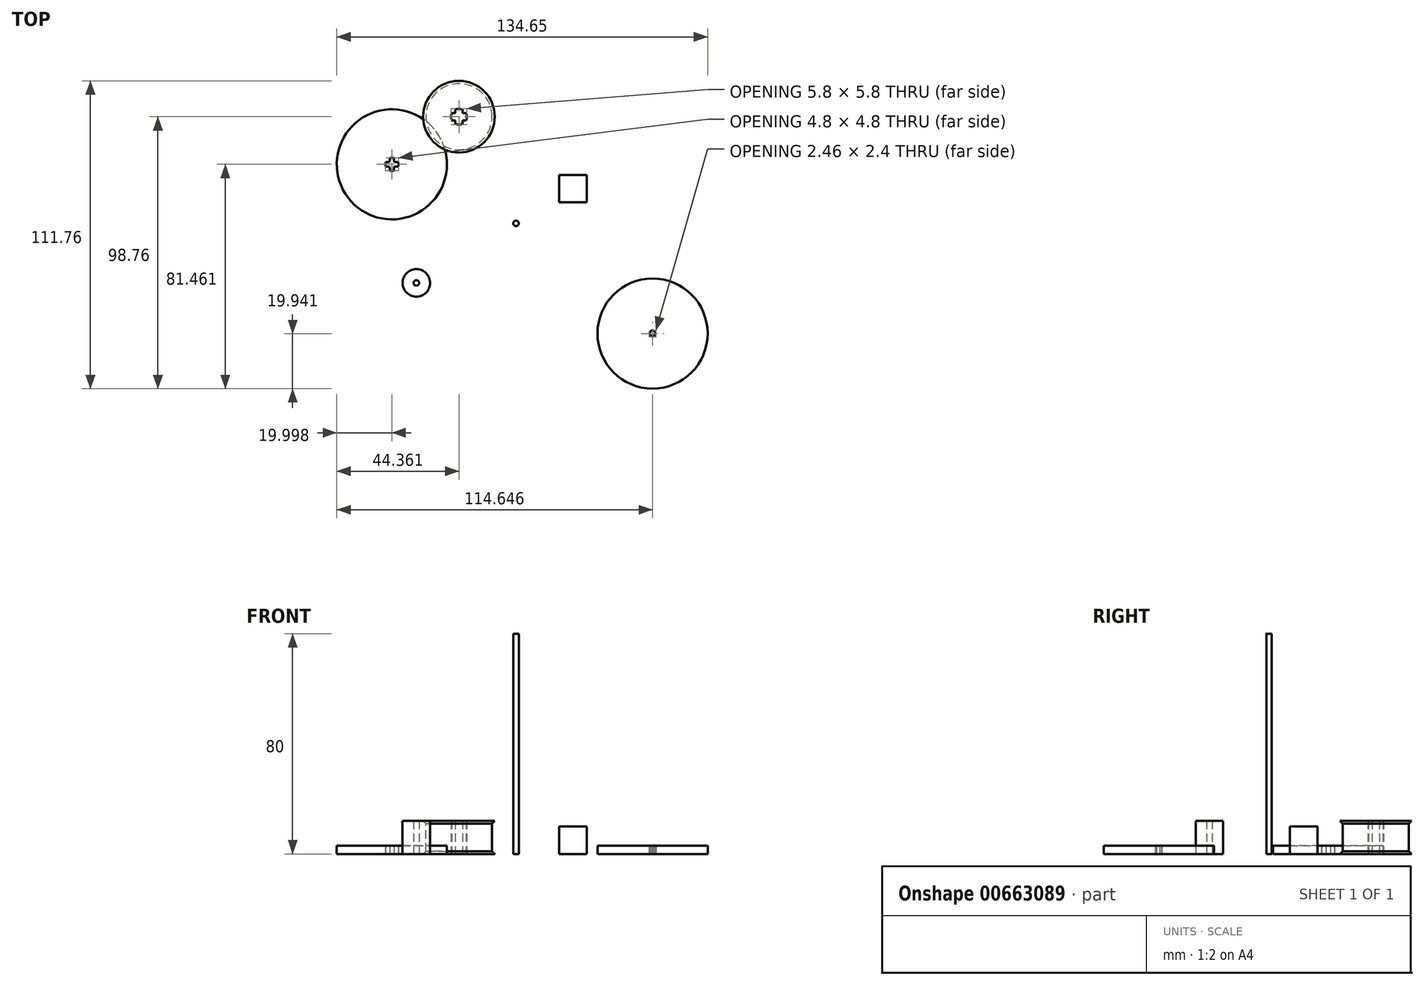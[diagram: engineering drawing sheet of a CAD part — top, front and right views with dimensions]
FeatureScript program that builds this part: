
annotation { "Feature Type Name" : "Feature", "Feature Type Description" : "" }
export const myFeature = defineFeature(function(context is Context, id is Id, definition is map)
    precondition{}
    {
        {
            var Q0;
            Q0=qCreatedBy(makeId("Top.planeOp"),FACE);
            var sketch = newSketch(context, id + "F0", { "sketchPlane" : qUnion([Q0])});
            skCircle(sketch, "E0", {"center": v(18.3, -78.76) * mm, "radius": 20 * mm});
            skCircle(sketch, "E1", {"center": v(18.3, -78.76) * mm, "radius": 0.97 * mm, "construction": true});
            skArc(sketch, "E2", {"start": v(17.76, -77.62) * mm, "mid": v(18.3, -77.78) * mm, "end": v(18.85, -77.62) * mm});
            skArc(sketch, "E3.1.0", {"start": v(17.07, -78.48) * mm, "mid": v(17.54, -78.15) * mm, "end": v(17.76, -77.62) * mm});
            skArc(sketch, "E3.2.0", {"start": v(17.32, -79.54) * mm, "mid": v(17.36, -78.97) * mm, "end": v(17.07, -78.48) * mm});
            skArc(sketch, "E3.3.0", {"start": v(18.3, -80.02) * mm, "mid": v(17.88, -79.64) * mm, "end": v(17.32, -79.54) * mm});
            skArc(sketch, "E3.4.0", {"start": v(19.3, -79.54) * mm, "mid": v(18.73, -79.64) * mm, "end": v(18.3, -80.02) * mm});
            skArc(sketch, "E3.5.0", {"start": v(19.54, -78.48) * mm, "mid": v(19.26, -78.97) * mm, "end": v(19.3, -79.54) * mm});
            skArc(sketch, "E3.6.0", {"start": v(18.85, -77.62) * mm, "mid": v(19.07, -78.15) * mm, "end": v(19.54, -78.48) * mm});
            skSolve(sketch);
        }
        {
            var Q0;
            Q0=makeQuery(id+"F0.imprint","IMPRINT",FACE,{"disambiguationData":[TD([[makeQuery(id+"F0.imprint","IMPRINT",EDGE,{"derivedFrom":sQuery(id+"F0.wireOp",EDGE,"E0")}),1.0]])]});
            extrude(context, id + "F1", {"entities" : qUnion([Q0]), "depth" : 3 * mm, "offsetDistance" : 25 * mm});
        }
        {
            var Q0;
            Q0=qCreatedBy(makeId("Top.planeOp"),FACE);
            var sketch = newSketch(context, id + "F2", { "sketchPlane" : qUnion([Q0])});
            skCircle(sketch, "E4", {"center": v(-31.27, -38.74) * mm, "radius": 1 * mm});
            skSolve(sketch);
        }
        {
            var Q0;
            Q0=makeQuery(id+"F2.imprint","IMPRINT",FACE,{"disambiguationData":[TD([[makeQuery(id+"F2.imprint","IMPRINT",EDGE,{"derivedFrom":sQuery(id+"F2.wireOp",EDGE,"E4")}),1.0]])]});
            extrude(context, id + "F3", {"entities" : qUnion([Q0]), "depth" : 80 * mm, "offsetDistance" : 25 * mm});
        }
        {
            var Q0;
            Q0=qCreatedBy(makeId("Top.planeOp"),FACE);
            var sketch = newSketch(context, id + "F4", { "sketchPlane" : qUnion([Q0])});
            skLineSegment(sketch, "E5.bottom", {"start": v(114.5, -144.93) * mm, "end": v(301.1, -144.93) * mm});
            skLineSegment(sketch, "E5.top", {"start": v(114.5, 146.95) * mm, "end": v(301.1, 146.95) * mm});
            skLineSegment(sketch, "E5.left", {"start": v(114.5, -144.93) * mm, "end": v(114.5, 146.95) * mm});
            skLineSegment(sketch, "E5.right", {"start": v(301.1, -144.93) * mm, "end": v(301.1, 146.95) * mm});
            skSolve(sketch);
        }
        {
            var Q0;
            Q0=makeQuery(id+"F4.imprint","IMPRINT",FACE,{"disambiguationData":[TD([[makeQuery(id+"F4.imprint","IMPRINT",EDGE,{"derivedFrom":sQuery(id+"F4.wireOp",EDGE,"E5.bottom")}),1.0]])]});
            extrude(context, id + "F5", {"entities" : qUnion([Q0]), "depth" : 308 * mm, "offsetDistance" : 25 * mm});
        }
        {
            var Q0;
            Q0=makeQuery(id+"F5.opExtrude","CAP_FACE",FACE,{"disambiguationData":[OSD([sQuery(id+"F4.wireOp",EDGE,"E5.bottom"),sQuery(id+"F4.wireOp",EDGE,"E5.top"),sQuery(id+"F4.wireOp",EDGE,"E5.left"),sQuery(id+"F4.wireOp",EDGE,"E5.right")])],"isStart":false});
            var Q1;
            Q1=makeQuery(id+"F5.opExtrude","CAP_FACE",FACE,{"disambiguationData":[OSD([sQuery(id+"F4.wireOp",EDGE,"E5.bottom"),sQuery(id+"F4.wireOp",EDGE,"E5.top"),sQuery(id+"F4.wireOp",EDGE,"E5.left"),sQuery(id+"F4.wireOp",EDGE,"E5.right")])],"isStart":true});
            shell(context, id + "F6", {"entities" : qUnion([Q0, Q1]), "thickness" : 2.5 * mm});
        }
        {
            var Q0;
            Q0=qCreatedBy(makeId("Top.planeOp"),FACE);
            var sketch = newSketch(context, id + "F7", { "sketchPlane" : qUnion([Q0])});
            skCircle(sketch, "E6", {"center": v(-67.45, -60.37) * mm, "radius": 5 * mm});
            skCircle(sketch, "E7", {"center": v(-67.45, -60.37) * mm, "radius": 1 * mm});
            skSolve(sketch);
        }
        {
            var Q0;
            Q0=makeQuery(id+"F7.imprint","IMPRINT",FACE,{"disambiguationData":[TD([[makeQuery(id+"F7.imprint","IMPRINT",EDGE,{"derivedFrom":sQuery(id+"F7.wireOp",EDGE,"E6")}),1.0]])]});
            extrude(context, id + "F8", {"entities" : qUnion([Q0]), "depth" : 12 * mm, "offsetDistance" : 25 * mm});
        }
        {
            var Q0;
            Q0=makeQuery(id+"F5.opExtrude","SWEPT_BODY",BODY,{"disambiguationData":[OSD([sQuery(id+"F4.wireOp",EDGE,"E5.bottom"),sQuery(id+"F4.wireOp",EDGE,"E5.top"),sQuery(id+"F4.wireOp",EDGE,"E5.left"),sQuery(id+"F4.wireOp",EDGE,"E5.right")])]});
            deleteBodies(context, id + "F9", {"entities" : qUnion([Q0])});
        }
        {
            var Q0;
            Q0=qCreatedBy(makeId("Front.planeOp"),FACE);
            var sketch = newSketch(context, id + "F10", { "sketchPlane" : qUnion([Q0])});
            skLineSegment(sketch, "E8", {"start": v(-51.98, 12) * mm, "end": v(-51.98, 0) * mm, "construction": true});
            skLineSegment(sketch, "E9", {"start": v(-51.98, 0) * mm, "end": v(-50.98, 0) * mm, "construction": true});
            skLineSegment(sketch, "E10", {"start": v(-39.98, 1) * mm, "end": v(-39.98, 11) * mm});
            skLineSegment(sketch, "E11", {"start": v(-38.98, 12) * mm, "end": v(-50.98, 12) * mm});
            skLineSegment(sketch, "E12", {"start": v(-38.98, 12) * mm, "end": v(-39.98, 11) * mm});
            skLineSegment(sketch, "E13", {"start": v(-39.98, 1) * mm, "end": v(-38.98, 0) * mm});
            skLineSegment(sketch, "E14", {"start": v(-50.98, 12) * mm, "end": v(-50.98, 0) * mm});
            skLineSegment(sketch, "E15", {"start": v(-50.98, 12) * mm, "end": v(-51.98, 12) * mm, "construction": true});
            skLineSegment(sketch, "E16", {"start": v(-50.98, 0) * mm, "end": v(-38.98, 0) * mm});
            skSolve(sketch);
        }
        {
            var Q0;
            Q0=makeQuery(id+"F10.imprint","IMPRINT",FACE,{"disambiguationData":[TD([[makeQuery(id+"F10.imprint","IMPRINT",EDGE,{"derivedFrom":sQuery(id+"F10.wireOp",EDGE,"E10")}),1.0]])]});
            var Q1;
            Q1=sQuery(id+"F10.wireOp",EDGE,"E8");
            revolve(context, id + "F11", {"surfaceOperationType" : NewSurfaceOperationType.NEW, "entities" : qUnion([Q0]), "axis" : qUnion([Q1]), "revolveType" : RevolveType.FULL});
        }
        {
            var Q0;
            Q0=makeQuery(id+"F11.opRevolve","SWEPT_FACE",FACE,{"disambiguationData":[OSD([sQuery(id+"F10.wireOp",EDGE,"E16")])]});
            var sketch = newSketch(context, id + "F12", { "sketchPlane" : qUnion([Q0])});
            skCircle(sketch, "E17.0", {"center": v(-51.98, 0) * mm, "radius": 13 * mm});
            skArc(sketch, "E18", {"start": v(-54.24, 0.8) * mm, "mid": v(-54.34, 0.4) * mm, "end": v(-54.38, 0) * mm, "construction": true});
            skLineSegment(sketch, "E19", {"start": v(-51.98, 2.4) * mm, "end": v(-51.98, -2.4) * mm, "construction": true});
            skLineSegment(sketch, "E20", {"start": v(-49.58, 0) * mm, "end": v(-54.38, 0) * mm, "construction": true});
            skLineSegment(sketch, "E21", {"start": v(-52.78, 2.26) * mm, "end": v(-52.78, 1.2) * mm, "construction": true});
            skLineSegment(sketch, "E22", {"start": v(-53.18, 0.8) * mm, "end": v(-54.24, 0.8) * mm, "construction": true});
            skArc(sketch, "E23.trimOffspring", {"start": v(-51.98, 2.4) * mm, "mid": v(-52.38, 2.37) * mm, "end": v(-52.78, 2.26) * mm, "construction": true});
            skPoint(sketch, "E24.visualSharp", {"position": v(-52.78, 0.8) * mm});
            skArc(sketch, "E24.filletArc", {"start": v(-53.18, 0.8) * mm, "mid": v(-52.9, 0.92) * mm, "end": v(-52.78, 1.2) * mm, "construction": true});
            skArc(sketch, "E25.1.0", {"start": v(-54.38, 0) * mm, "mid": v(-54.34, -0.4) * mm, "end": v(-54.24, -0.8) * mm, "construction": true});
            skLineSegment(sketch, "E25.1.1", {"start": v(-54.24, -0.8) * mm, "end": v(-53.18, -0.8) * mm, "construction": true});
            skArc(sketch, "E25.1.2", {"start": v(-52.78, -1.2) * mm, "mid": v(-52.9, -0.92) * mm, "end": v(-53.18, -0.8) * mm, "construction": true});
            skLineSegment(sketch, "E25.1.3", {"start": v(-52.78, -1.2) * mm, "end": v(-52.78, -2.26) * mm, "construction": true});
            skArc(sketch, "E25.1.4", {"start": v(-52.78, -2.26) * mm, "mid": v(-52.38, -2.37) * mm, "end": v(-51.98, -2.4) * mm, "construction": true});
            skArc(sketch, "E25.2.0", {"start": v(-51.98, -2.4) * mm, "mid": v(-51.57, -2.37) * mm, "end": v(-51.18, -2.26) * mm, "construction": true});
            skLineSegment(sketch, "E25.2.1", {"start": v(-51.18, -2.26) * mm, "end": v(-51.18, -1.2) * mm, "construction": true});
            skArc(sketch, "E25.2.2", {"start": v(-50.78, -0.8) * mm, "mid": v(-51.06, -0.92) * mm, "end": v(-51.18, -1.2) * mm, "construction": true});
            skLineSegment(sketch, "E25.2.3", {"start": v(-50.78, -0.8) * mm, "end": v(-49.72, -0.8) * mm, "construction": true});
            skArc(sketch, "E25.2.4", {"start": v(-49.72, -0.8) * mm, "mid": v(-49.61, -0.4) * mm, "end": v(-49.58, 0) * mm, "construction": true});
            skArc(sketch, "E25.3.0", {"start": v(-49.58, 0) * mm, "mid": v(-49.61, 0.4) * mm, "end": v(-49.72, 0.8) * mm, "construction": true});
            skLineSegment(sketch, "E25.3.1", {"start": v(-49.72, 0.8) * mm, "end": v(-50.78, 0.8) * mm, "construction": true});
            skArc(sketch, "E25.3.2", {"start": v(-51.18, 1.2) * mm, "mid": v(-51.06, 0.92) * mm, "end": v(-50.78, 0.8) * mm, "construction": true});
            skLineSegment(sketch, "E25.3.3", {"start": v(-51.18, 1.2) * mm, "end": v(-51.18, 2.26) * mm, "construction": true});
            skArc(sketch, "E25.3.4", {"start": v(-51.18, 2.26) * mm, "mid": v(-51.57, 2.37) * mm, "end": v(-51.98, 2.4) * mm, "construction": true});
            skArc(sketch, "E26.0", {"start": v(-50.68, 2.6) * mm, "mid": v(-51.31, 2.82) * mm, "end": v(-51.98, 2.9) * mm});
            skLineSegment(sketch, "E26.1", {"start": v(-50.68, 1.3) * mm, "end": v(-50.68, 2.6) * mm});
            skLineSegment(sketch, "E26.2", {"start": v(-49.39, 1.3) * mm, "end": v(-50.68, 1.3) * mm});
            skArc(sketch, "E26.3", {"start": v(-49.08, 0) * mm, "mid": v(-49.16, 0.67) * mm, "end": v(-49.39, 1.3) * mm});
            skArc(sketch, "E26.4", {"start": v(-49.39, -1.3) * mm, "mid": v(-49.16, -0.67) * mm, "end": v(-49.08, 0) * mm});
            skArc(sketch, "E26.5", {"start": v(-54.88, 0) * mm, "mid": v(-54.8, -0.67) * mm, "end": v(-54.57, -1.3) * mm});
            skArc(sketch, "E26.6", {"start": v(-54.57, 1.3) * mm, "mid": v(-54.8, 0.67) * mm, "end": v(-54.88, 0) * mm});
            skLineSegment(sketch, "E26.7", {"start": v(-53.28, 1.3) * mm, "end": v(-54.57, 1.3) * mm});
            skLineSegment(sketch, "E26.8", {"start": v(-53.28, 2.6) * mm, "end": v(-53.28, 1.3) * mm});
            skLineSegment(sketch, "E26.9", {"start": v(-54.57, -1.3) * mm, "end": v(-53.28, -1.3) * mm});
            skLineSegment(sketch, "E26.10", {"start": v(-53.28, -1.3) * mm, "end": v(-53.28, -2.6) * mm});
            skArc(sketch, "E26.11", {"start": v(-53.28, -2.6) * mm, "mid": v(-52.65, -2.82) * mm, "end": v(-51.98, -2.9) * mm});
            skArc(sketch, "E26.12", {"start": v(-51.98, -2.9) * mm, "mid": v(-51.31, -2.82) * mm, "end": v(-50.68, -2.6) * mm});
            skLineSegment(sketch, "E26.13", {"start": v(-50.68, -2.6) * mm, "end": v(-50.68, -1.3) * mm});
            skArc(sketch, "E26.14", {"start": v(-51.98, 2.9) * mm, "mid": v(-52.65, 2.82) * mm, "end": v(-53.28, 2.6) * mm});
            skLineSegment(sketch, "E26.15", {"start": v(-50.68, -1.3) * mm, "end": v(-49.39, -1.3) * mm});
            skSolve(sketch);
        }
        {
            var Q0;
            Q0=makeQuery(id+"F12.imprint","IMPRINT",FACE,{"disambiguationData":[TD([[makeQuery(id+"F12.imprint","IMPRINT",EDGE,{"derivedFrom":sQuery(id+"F12.wireOp",EDGE,"E26.0")}),1.0]])]});
            extrude(context, id + "F13", {"entities" : qUnion([Q0]), "operationType" : NewBodyOperationType.REMOVE, "endBound" : BoundingType.THROUGH_ALL, "oppositeDirection" : true, "depth" : 8 * mm, "offsetDistance" : 25 * mm});
        }
        {
            var Q0;
            Q0=qCreatedBy(makeId("Top.planeOp"),FACE);
            var sketch = newSketch(context, id + "F14", { "sketchPlane" : qUnion([Q0])});
            skArc(sketch, "E27", {"start": v(-78.6, -16.5) * mm, "mid": v(-78.7, -16.9) * mm, "end": v(-78.74, -17.3) * mm});
            skLineSegment(sketch, "E28", {"start": v(-76.34, -14.9) * mm, "end": v(-76.34, -19.7) * mm, "construction": true});
            skLineSegment(sketch, "E29", {"start": v(-73.94, -17.3) * mm, "end": v(-78.74, -17.3) * mm, "construction": true});
            skLineSegment(sketch, "E30", {"start": v(-77.14, -15.04) * mm, "end": v(-77.14, -16.1) * mm});
            skLineSegment(sketch, "E31", {"start": v(-77.54, -16.5) * mm, "end": v(-78.6, -16.5) * mm});
            skArc(sketch, "E32.trimOffspring", {"start": v(-76.34, -14.9) * mm, "mid": v(-76.75, -14.93) * mm, "end": v(-77.14, -15.04) * mm});
            skPoint(sketch, "E33.visualSharp", {"position": v(-77.14, -16.5) * mm});
            skArc(sketch, "E33.filletArc", {"start": v(-77.54, -16.5) * mm, "mid": v(-77.26, -16.38) * mm, "end": v(-77.14, -16.1) * mm});
            skArc(sketch, "E34.1.0", {"start": v(-78.74, -17.3) * mm, "mid": v(-78.7, -17.7) * mm, "end": v(-78.6, -18.1) * mm});
            skLineSegment(sketch, "E34.1.1", {"start": v(-78.6, -18.1) * mm, "end": v(-77.54, -18.1) * mm});
            skArc(sketch, "E34.1.2", {"start": v(-77.14, -18.5) * mm, "mid": v(-77.26, -18.22) * mm, "end": v(-77.54, -18.1) * mm});
            skLineSegment(sketch, "E34.1.3", {"start": v(-77.14, -18.5) * mm, "end": v(-77.14, -19.56) * mm});
            skArc(sketch, "E34.1.4", {"start": v(-77.14, -19.56) * mm, "mid": v(-76.75, -19.66) * mm, "end": v(-76.34, -19.7) * mm});
            skArc(sketch, "E34.2.0", {"start": v(-76.34, -19.7) * mm, "mid": v(-75.94, -19.66) * mm, "end": v(-75.54, -19.56) * mm});
            skLineSegment(sketch, "E34.2.1", {"start": v(-75.54, -19.56) * mm, "end": v(-75.54, -18.5) * mm});
            skArc(sketch, "E34.2.2", {"start": v(-75.14, -18.1) * mm, "mid": v(-75.43, -18.22) * mm, "end": v(-75.54, -18.5) * mm});
            skLineSegment(sketch, "E34.2.3", {"start": v(-75.14, -18.1) * mm, "end": v(-74.08, -18.1) * mm});
            skArc(sketch, "E34.2.4", {"start": v(-74.08, -18.1) * mm, "mid": v(-73.98, -17.7) * mm, "end": v(-73.94, -17.3) * mm});
            skArc(sketch, "E34.3.0", {"start": v(-73.94, -17.3) * mm, "mid": v(-73.98, -16.9) * mm, "end": v(-74.08, -16.5) * mm});
            skLineSegment(sketch, "E34.3.1", {"start": v(-74.08, -16.5) * mm, "end": v(-75.14, -16.5) * mm});
            skArc(sketch, "E34.3.2", {"start": v(-75.54, -16.1) * mm, "mid": v(-75.43, -16.38) * mm, "end": v(-75.14, -16.5) * mm});
            skLineSegment(sketch, "E34.3.3", {"start": v(-75.54, -16.1) * mm, "end": v(-75.54, -15.04) * mm});
            skArc(sketch, "E34.3.4", {"start": v(-75.54, -15.04) * mm, "mid": v(-75.94, -14.93) * mm, "end": v(-76.34, -14.9) * mm});
            skCircle(sketch, "E35", {"center": v(-76.34, -17.3) * mm, "radius": 20 * mm});
            skSolve(sketch);
        }
        {
            var Q0;
            Q0=makeQuery(id+"F14.imprint","IMPRINT",FACE,{"disambiguationData":[TD([[makeQuery(id+"F14.imprint","IMPRINT",EDGE,{"derivedFrom":sQuery(id+"F14.wireOp",EDGE,"E27")}),-1.0]])]});
            extrude(context, id + "F15", {"entities" : qUnion([Q0]), "depth" : 3 * mm, "offsetDistance" : 25 * mm});
        }
        {
            var Q0;
            Q0=qCreatedBy(makeId("Top.planeOp"),FACE);
            var sketch = newSketch(context, id + "F16", { "sketchPlane" : qUnion([Q0])});
            skLineSegment(sketch, "E36.bottom", {"start": v(-15.58, -21.12) * mm, "end": v(-5.58, -21.12) * mm});
            skLineSegment(sketch, "E36.top", {"start": v(-15.58, -31.12) * mm, "end": v(-5.58, -31.12) * mm});
            skLineSegment(sketch, "E36.left", {"start": v(-15.58, -21.12) * mm, "end": v(-15.58, -31.12) * mm});
            skLineSegment(sketch, "E36.right", {"start": v(-5.58, -21.12) * mm, "end": v(-5.58, -31.12) * mm});
            skSolve(sketch);
        }
        {
            var Q0;
            Q0 = qSketchRegion(id + "F16", true);
            extrude(context, id + "F17", {"entities" : qUnion([Q0]), "depth" : 10 * mm, "offsetDistance" : 25 * mm});
        }
    });
